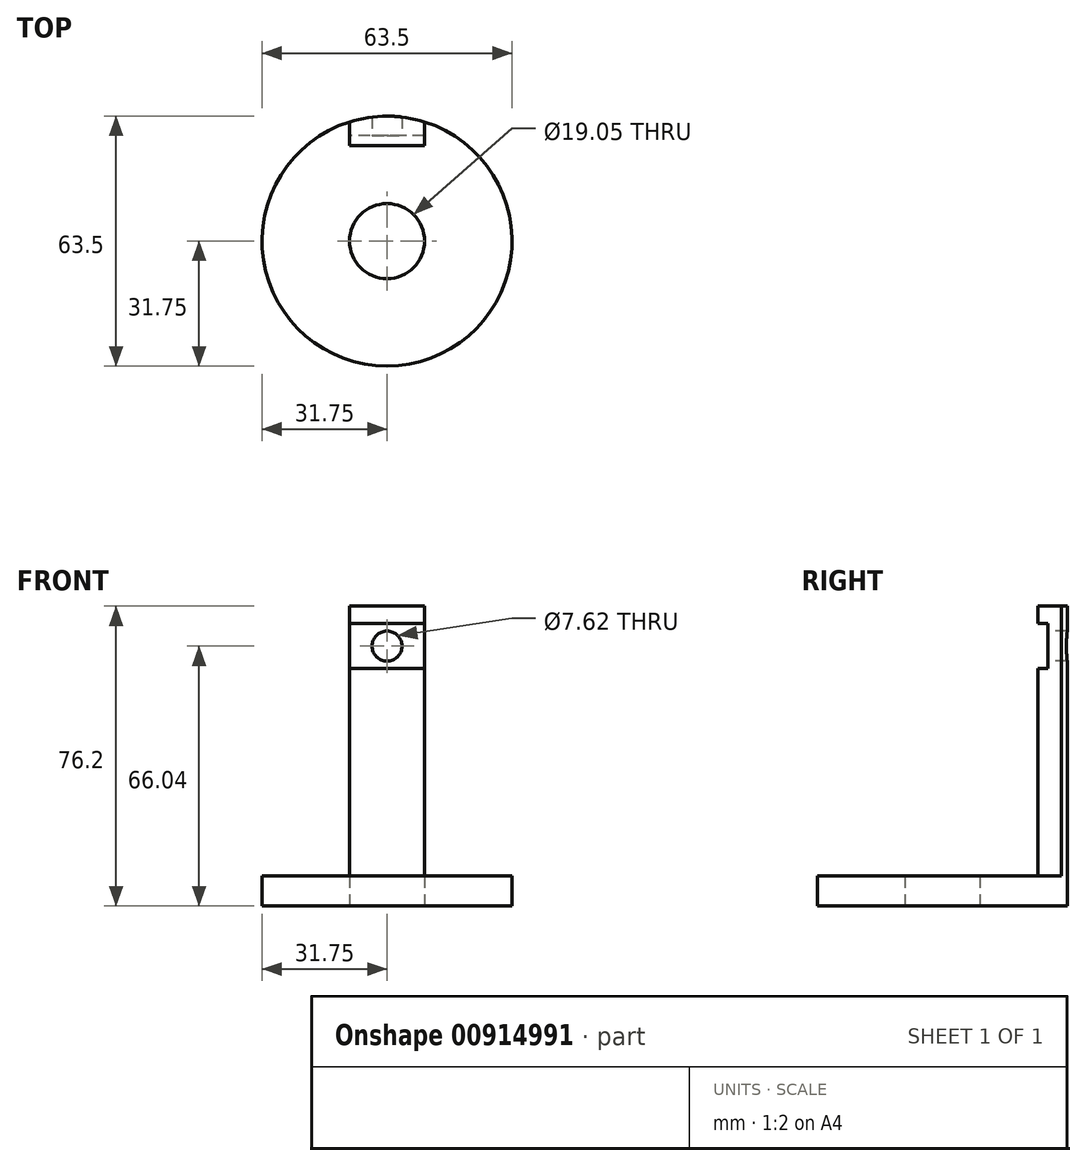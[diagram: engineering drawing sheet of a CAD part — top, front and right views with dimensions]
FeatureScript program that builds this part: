
annotation { "Feature Type Name" : "Feature", "Feature Type Description" : "" }
export const myFeature = defineFeature(function(context is Context, id is Id, definition is map)
    precondition{}
    {
        {
            var Q0;
            Q0=qCreatedBy(makeId("Top.planeOp"),FACE);
            var sketch = newSketch(context, id + "F0", { "sketchPlane" : qUnion([Q0])});
            skCircle(sketch, "E0", {"center": v(0, 0) * mm, "radius": 31.75 * mm});
            skLineSegment(sketch, "E1.bottom", {"start": v(9.52, 21.63) * mm, "end": v(-9.52, 21.63) * mm});
            skLineSegment(sketch, "E1.top", {"start": v(9.53, 41.87) * mm, "end": v(-9.53, 41.87) * mm});
            skLineSegment(sketch, "E1.left", {"start": v(9.53, 21.63) * mm, "end": v(9.53, 41.87) * mm});
            skLineSegment(sketch, "E1.right", {"start": v(-9.52, 21.63) * mm, "end": v(-9.52, 41.87) * mm});
            skPoint(sketch, "E1.middle", {"position": v(0, 31.75) * mm});
            skLineSegment(sketch, "E2", {"start": v(0, 31.75) * mm, "end": v(0, 41.87) * mm, "construction": true});
            skCircle(sketch, "E3", {"center": v(0, 0) * mm, "radius": 9.53 * mm});
            skLineSegment(sketch, "E4", {"start": v(-9.52, 24.23) * mm, "end": v(9.53, 24.23) * mm});
            skSolve(sketch);
        }
        {
            var Q0;
            Q0=makeQuery(id+"F0.imprint","IMPRINT",FACE,{"disambiguationData":[TD([[makeQuery(id+"F0.imprint","IMPRINT",EDGE,{"derivedFrom":sQuery(id+"F0.wireOp",EDGE,"E0")}),1.0]])]});
            var Q1;
            {var subQ1=sQuery(id+"F0.wireOp",EDGE,"E1.bottom");Q1=makeQuery(id+"F0.imprint","IMPRINT",FACE,{"disambiguationData":[TD([[makeQuery(id+"F0.imprint","IMPRINT",EDGE,{"derivedFrom":subQ1}),1.0]])]});}
            var Q2;
            {var subQ0=sQuery(id+"F0.wireOp",EDGE,"E1.bottom");Q2=makeQuery(id+"F0.imprint","IMPRINT",FACE,{"disambiguationData":[TD([[makeQuery(id+"F0.imprint","IMPRINT",EDGE,{"derivedFrom":subQ0}),-1.0]])]});}
            extrude(context, id + "F1", {"entities" : qUnion([Q0, Q1, Q2]), "depth" : 7.62 * mm, "offsetDistance" : 25.4 * mm});
        }
        {
            var Q0;
            {var subQ5=sQuery(id+"F0.wireOp",EDGE,"E4");Q0=makeQuery(id+"F0.imprint","IMPRINT",FACE,{"disambiguationData":[TD([[makeQuery(id+"F0.imprint","IMPRINT",EDGE,{"derivedFrom":subQ5}),1.0]])]});}
            extrude(context, id + "F2", {"entities" : qUnion([Q0]), "operationType" : NewBodyOperationType.ADD, "depth" : 76.2 * mm, "offsetDistance" : 25.4 * mm});
        }
        {
            var Q0;
            Q0=makeQuery(id+"F2.opExtrude","SWEPT_FACE",FACE,{"disambiguationData":[OSD([sQuery(id+"F0.wireOp",EDGE,"E4")])]});
            var sketch = newSketch(context, id + "F3", { "sketchPlane" : qUnion([Q0])});
            skCircle(sketch, "E5", {"center": v(0, 66.04) * mm, "radius": 3.81 * mm});
            skLineSegment(sketch, "E6", {"start": v(9.53, 60.33) * mm, "end": v(-9.52, 60.33) * mm});
            skLineSegment(sketch, "E7", {"start": v(9.53, 71.75) * mm, "end": v(-9.52, 71.75) * mm});
            skSolve(sketch);
        }
        {
            var Q0;
            Q0=makeQuery(id+"F3.imprint","IMPRINT",FACE,{"disambiguationData":[TD([[makeQuery(id+"F3.imprint","IMPRINT",EDGE,{"derivedFrom":sQuery(id+"F3.wireOp",EDGE,"E5")}),1.0]])]});
            extrude(context, id + "F4", {"entities" : qUnion([Q0]), "operationType" : NewBodyOperationType.REMOVE, "oppositeDirection" : true, "depth" : 25.4 * mm, "offsetDistance" : 25.4 * mm});
        }
        {
            var Q0;
            Q0=makeQuery(id+"F3.imprint","IMPRINT",FACE,{"disambiguationData":[TD([[makeQuery(id+"F3.imprint","IMPRINT",EDGE,{"derivedFrom":sQuery(id+"F3.wireOp",EDGE,"E5")}),-1.0]])]});
            extrude(context, id + "F5", {"entities" : qUnion([Q0]), "operationType" : NewBodyOperationType.REMOVE, "oppositeDirection" : true, "depth" : 2.54 * mm, "offsetDistance" : 25.4 * mm});
        }
    });
